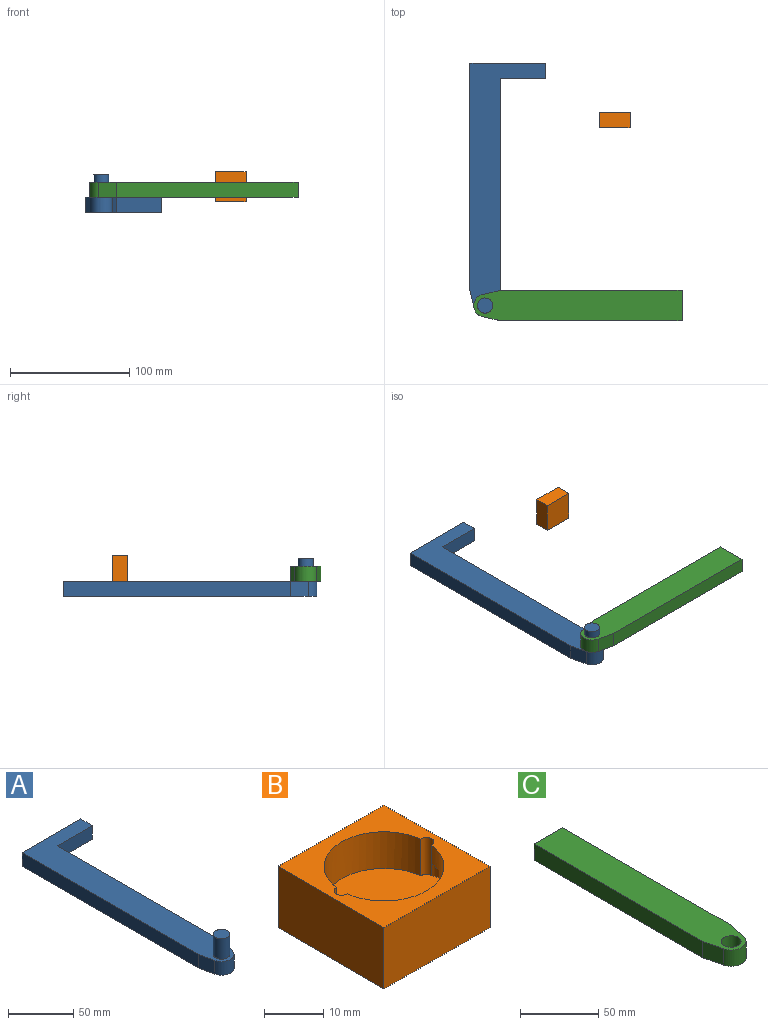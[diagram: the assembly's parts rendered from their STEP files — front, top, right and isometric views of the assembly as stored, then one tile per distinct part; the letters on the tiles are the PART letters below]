
ASSEMBLY  parts=3 mates=1
PART A: 12 faces, bbox 63.5x212.7x31.8 mm
  f0: plane 177.8x12.7mm, normal (1,0,0), area 2258.1mm2, adj f1,f7,f8,f9
  f1: plane 38.1x12.7mm, normal (0,-1,0), area 483.9mm2, adj f0,f2,f8,f9
  f2: plane 12.7x12.7mm, normal (1,0,0), area 161.3mm2, adj f1,f3,f8,f9
  f3: plane 63.5x12.7mm, normal (0,1,0), area 806.5mm2, adj f2,f4,f8,f9
  f4: plane 190.5x12.7mm, normal (-1,0,0), area 2419.3mm2, adj f3,f5,f8,f9
  f5: plane 14.84x12.7mm, normal (-0.97,-0.22,0), area 193.4mm2, adj f4,f6,f8,f9
  f6: cylinder r=9.53mm len=18.56mm, axis (0,0,-1), area 325.3mm2, adj f5,f7,f8,f9
  f7: plane 14.84x12.7mm, normal (0.97,-0.22,0), area 193.4mm2, adj f0,f6,f8,f9
  f8: plane 212.73x63.5mm, normal (0,0,1), area 5624.2mm2, adj f0,f1,f2,f3,f4,f5,f6,f7
  f9: plane 212.73x63.5mm, normal (0,0,-1), area 5750.9mm2, adj f0,f1,f2,f3,f4,f5,f6,f7
  f10: cylinder r=6.35mm len=19.05mm, axis (0,0,-1), area 760.1mm2, adj f8,f11
  f11: plane 12.7x12.7mm, normal (0,0,1), area 126.7mm2, adj f10
PART B: 16 faces, bbox 25.4x25.4x12.7 mm
  f0: cylinder r=10.16mm len=20.16mm, axis (0,0,1), area 212.7mm2, adj f1,f7,f9,f10,f11,f13,f14,f15
  f1: cylinder r=1.27mm len=7.62mm, axis (0,0,1), area 23.8mm2, adj f0,f2,f7,f10,f14,f15
  f2: cylinder r=10.16mm len=20.16mm, axis (0,0,1), area 215.7mm2, adj f1,f7,f9,f10,f12,f13
  f3: plane 25.4x12.7mm, normal (0,-1,0), area 322.6mm2, adj f4,f6,f7,f8
  f4: plane 25.4x12.7mm, normal (1,0,0), area 322.6mm2, adj f3,f5,f7,f8
  f5: plane 25.4x12.7mm, normal (0,1,0), area 322.6mm2, adj f4,f6,f7,f8
  f6: plane 25.4x12.7mm, normal (-1,0,0), area 322.6mm2, adj f3,f5,f7,f8
  f7: plane 25.4x25.4mm, normal (0,0,1), area 315.7mm2, adj f0,f1,f2,f3,f4,f5,f6,f9
  f8: plane 25.4x25.4mm, normal (0,0,-1), area 645.2mm2, adj f3,f4,f5,f6
  f9: cylinder r=1.27mm len=3.81mm, axis (0,0,1), area 15.8mm2, adj f0,f2,f7,f11,f12
  f10: plane 23.5x20.32mm, normal (0,0,1), area 337.1mm2, adj f0,f1,f2,f13,f15
  f11: plane 1.07x0.71mm, normal (0,0,-1), area 0.1mm2, adj f0,f9,f13
  f12: plane 4.2x2.16mm, normal (0,0,-1), area 3.4mm2, adj f2,f9,f13
  f13: cylinder r=2.54mm len=4.91mm, axis (0,0,-1), area 25.7mm2, adj f0,f2,f10,f11,f12
  f14: plane 3.77x2.33mm, normal (0,0,-1), area 4.2mm2, adj f0,f1,f15
  f15: cylinder r=2.54mm len=3.81mm, axis (0,0,-1), area 19.3mm2, adj f0,f1,f10,f14
PART C: 9 faces, bbox 25.4x174.6x12.7 mm
  f0: plane 25.4x12.7mm, normal (0,1,0), area 322.6mm2, adj f1,f5,f7,f8
  f1: plane 152.4x12.7mm, normal (-1,0,0), area 1935.5mm2, adj f0,f2,f7,f8
  f2: plane 14.84x12.7mm, normal (-0.97,-0.22,0), area 193.4mm2, adj f1,f3,f7,f8
  f3: cylinder r=9.53mm len=18.56mm, axis (0,0,-1), area 325.3mm2, adj f2,f4,f7,f8
  f4: plane 14.84x12.7mm, normal (0.97,-0.22,0), area 193.4mm2, adj f3,f5,f7,f8
  f5: plane 152.4x12.7mm, normal (1,0,0), area 1935.5mm2, adj f0,f4,f7,f8
  f6: cylinder r=6.35mm len=12.7mm, axis (0,0,-1), area 506.7mm2, adj f7,f8
  f7: plane 174.63x25.4mm, normal (0,0,1), area 4172.6mm2, adj f0,f1,f2,f3,f4,f5,f6
  f8: plane 174.63x25.4mm, normal (0,0,-1), area 4172.6mm2, adj f0,f1,f2,f3,f4,f5,f6
PLACE A rot(axis=(-0.66,0.75,0),0deg) t=(-122.11,-39.81,60.79)mm
PLACE B rot(axis=(-1,0,0),90deg) t=(-13.32,20.28,82.15)mm
PLACE C rot(axis=(0,0,-1),90deg) t=(-33.25,-128.66,73.49)mm
MATE fastened A.f10 <-> C.f6  axis (0,0,-1) through (-122.11,-128.66,73.49)mm
